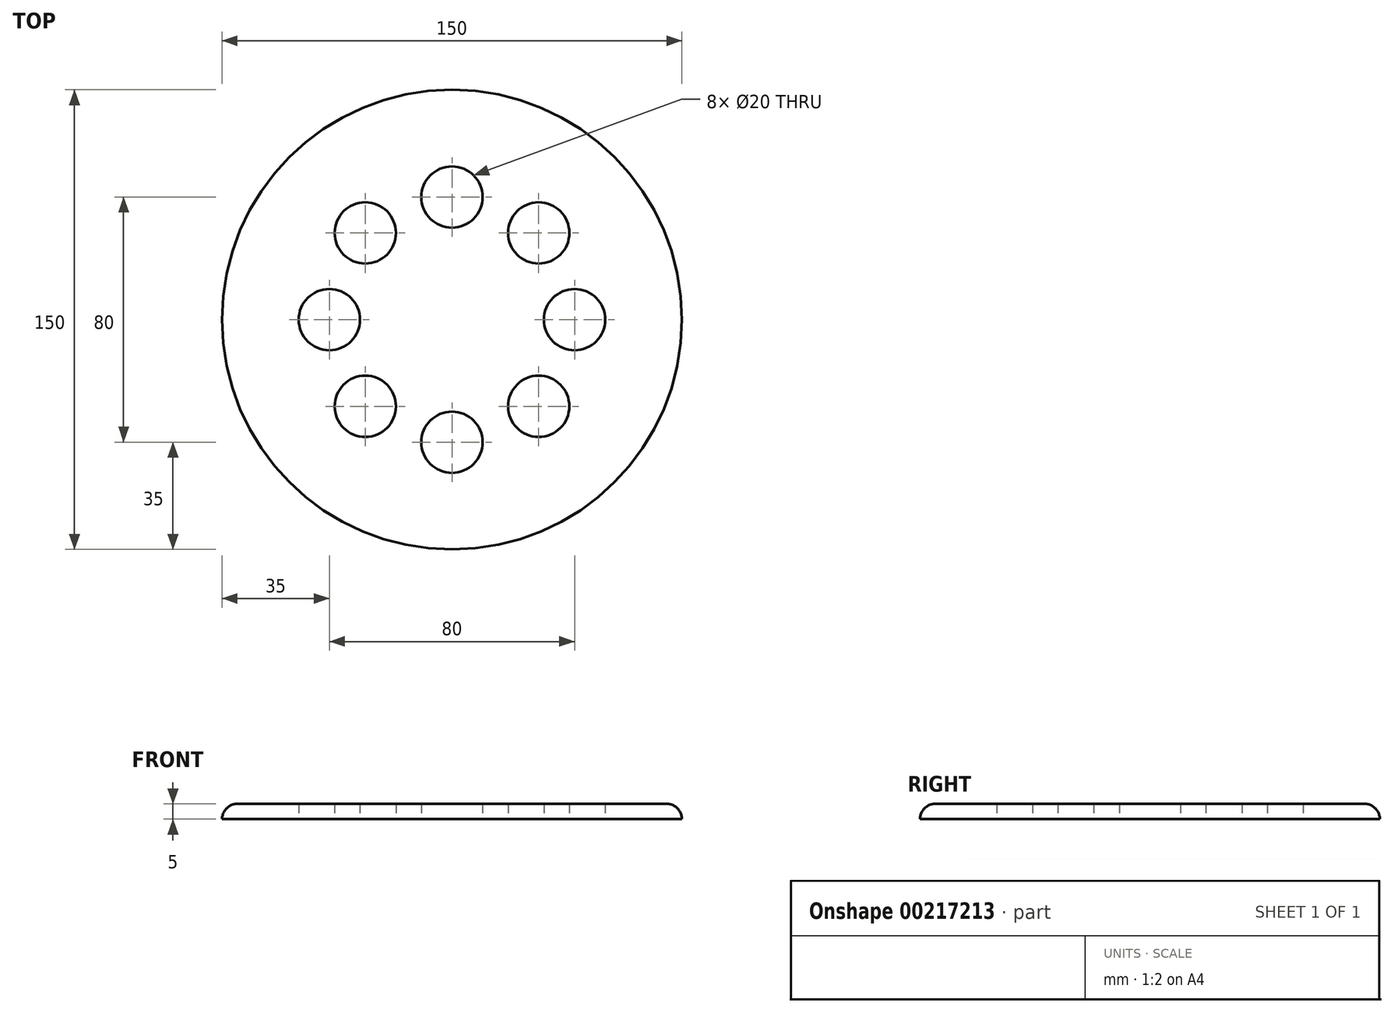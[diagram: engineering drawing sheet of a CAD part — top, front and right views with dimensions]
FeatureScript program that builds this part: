
annotation { "Feature Type Name" : "Feature", "Feature Type Description" : "" }
export const myFeature = defineFeature(function(context is Context, id is Id, definition is map)
    precondition{}
    {
        {
            var Q0;
            Q0=qCreatedBy(makeId("Top.planeOp"),FACE);
            var sketch = newSketch(context, id + "F0", { "sketchPlane" : qUnion([Q0])});
            skCircle(sketch, "E0", {"center": v(0, 0) * mm, "radius": 75 * mm});
            skSolve(sketch);
        }
        {
            var Q0;
            Q0=makeQuery(id+"F0.imprint","IMPRINT",FACE,{"disambiguationData":[TD([[makeQuery(id+"F0.imprint","IMPRINT",EDGE,{"derivedFrom":sQuery(id+"F0.wireOp",EDGE,"E0")}),1.0]])]});
            var sketch = newSketch(context, id + "F1", { "sketchPlane" : qUnion([Q0])});
            skCircle(sketch, "E1", {"center": v(0, 40) * mm, "radius": 10 * mm});
            skCircle(sketch, "E2.1.0", {"center": v(-28.28, 28.28) * mm, "radius": 10 * mm});
            skCircle(sketch, "E2.2.0", {"center": v(-40, 0) * mm, "radius": 10 * mm});
            skCircle(sketch, "E2.3.0", {"center": v(-28.28, -28.28) * mm, "radius": 10 * mm});
            skCircle(sketch, "E2.4.0", {"center": v(0, -40) * mm, "radius": 10 * mm});
            skCircle(sketch, "E2.5.0", {"center": v(28.28, -28.28) * mm, "radius": 10 * mm});
            skCircle(sketch, "E2.6.0", {"center": v(40, 0) * mm, "radius": 10 * mm});
            skCircle(sketch, "E2.7.0", {"center": v(28.28, 28.28) * mm, "radius": 10 * mm});
            skPoint(sketch, "E2.center", {"position": v(0, 0) * mm});
            skCircle(sketch, "E3", {"center": v(-19.19, -43.45) * mm, "radius": 7.5 * mm});
            skCircle(sketch, "E4.1.0", {"center": v(43.45, -19.19) * mm, "radius": 7.5 * mm});
            skCircle(sketch, "E4.2.0", {"center": v(19.19, 43.45) * mm, "radius": 7.5 * mm});
            skCircle(sketch, "E4.3.0", {"center": v(-43.45, 19.19) * mm, "radius": 7.5 * mm});
            skSolve(sketch);
        }
        {
            var Q0;
            Q0=makeQuery(id+"F0.imprint","IMPRINT",FACE,{"disambiguationData":[TD([[makeQuery(id+"F0.imprint","IMPRINT",EDGE,{"derivedFrom":sQuery(id+"F0.wireOp",EDGE,"E0")}),1.0]])]});
            extrude(context, id + "F2", {"entities" : qUnion([Q0]), "depth" : 5 * mm});
        }
        {
            var Q0;
            Q0=makeQuery(id+"F2.opExtrude","CAP_EDGE",EDGE,{"disambiguationData":[OSD([sQuery(id+"F0.wireOp",EDGE,"E0")])],"isStart":false});
            fillet(context, id + "F3", {"entities" : qUnion([Q0]), "radius" : 5 * mm, "tangentPropagation" : true, "allowEdgeOverflow" : false});
        }
        {
            var Q0;
            Q0=sQuery(id+"F1.wireOp",EDGE,"E4.3.0");
            var Q1;
            Q1=sQuery(id+"F1.wireOp",EDGE,"E3");
            var Q2;
            Q2=sQuery(id+"F1.wireOp",EDGE,"E4.1.0");
            var Q3;
            Q3=sQuery(id+"F1.wireOp",EDGE,"E4.2.0");
            extrude(context, id + "F4", {"bodyType" : ToolBodyType.SURFACE, "surfaceEntities" : qUnion([Q0, Q1, Q2, Q3]), "oppositeDirection" : true, "depth" : 100 * mm});
        }
        {
            var Q0;
            Q0=makeQuery(id+"F1.imprint","IMPRINT",FACE,{"disambiguationData":[TD([[makeQuery(id+"F1.imprint","IMPRINT",EDGE,{"derivedFrom":sQuery(id+"F1.wireOp",EDGE,"E2.4.0")}),1.0]])]});
            var Q1;
            Q1=makeQuery(id+"F1.imprint","IMPRINT",FACE,{"disambiguationData":[TD([[makeQuery(id+"F1.imprint","IMPRINT",EDGE,{"derivedFrom":sQuery(id+"F1.wireOp",EDGE,"E2.5.0")}),1.0]])]});
            var Q2;
            Q2=makeQuery(id+"F1.imprint","IMPRINT",FACE,{"disambiguationData":[TD([[makeQuery(id+"F1.imprint","IMPRINT",EDGE,{"derivedFrom":sQuery(id+"F1.wireOp",EDGE,"E2.3.0")}),1.0]])]});
            var Q3;
            Q3=makeQuery(id+"F1.imprint","IMPRINT",FACE,{"disambiguationData":[TD([[makeQuery(id+"F1.imprint","IMPRINT",EDGE,{"derivedFrom":sQuery(id+"F1.wireOp",EDGE,"E2.2.0")}),1.0]])]});
            var Q4;
            Q4=makeQuery(id+"F1.imprint","IMPRINT",FACE,{"disambiguationData":[TD([[makeQuery(id+"F1.imprint","IMPRINT",EDGE,{"derivedFrom":sQuery(id+"F1.wireOp",EDGE,"E2.1.0")}),1.0]])]});
            var Q5;
            Q5=makeQuery(id+"F1.imprint","IMPRINT",FACE,{"disambiguationData":[TD([[makeQuery(id+"F1.imprint","IMPRINT",EDGE,{"derivedFrom":sQuery(id+"F1.wireOp",EDGE,"E1")}),1.0]])]});
            var Q6;
            Q6=makeQuery(id+"F1.imprint","IMPRINT",FACE,{"disambiguationData":[TD([[makeQuery(id+"F1.imprint","IMPRINT",EDGE,{"derivedFrom":sQuery(id+"F1.wireOp",EDGE,"E2.7.0")}),1.0]])]});
            var Q7;
            Q7=makeQuery(id+"F1.imprint","IMPRINT",FACE,{"disambiguationData":[TD([[makeQuery(id+"F1.imprint","IMPRINT",EDGE,{"derivedFrom":sQuery(id+"F1.wireOp",EDGE,"E2.6.0")}),1.0]])]});
            extrude(context, id + "F5", {"entities" : qUnion([Q0, Q1, Q2, Q3, Q4, Q5, Q6, Q7]), "operationType" : NewBodyOperationType.REMOVE, "endBound" : BoundingType.UP_TO_NEXT, "depth" : 2.2 * mm});
        }
    });
